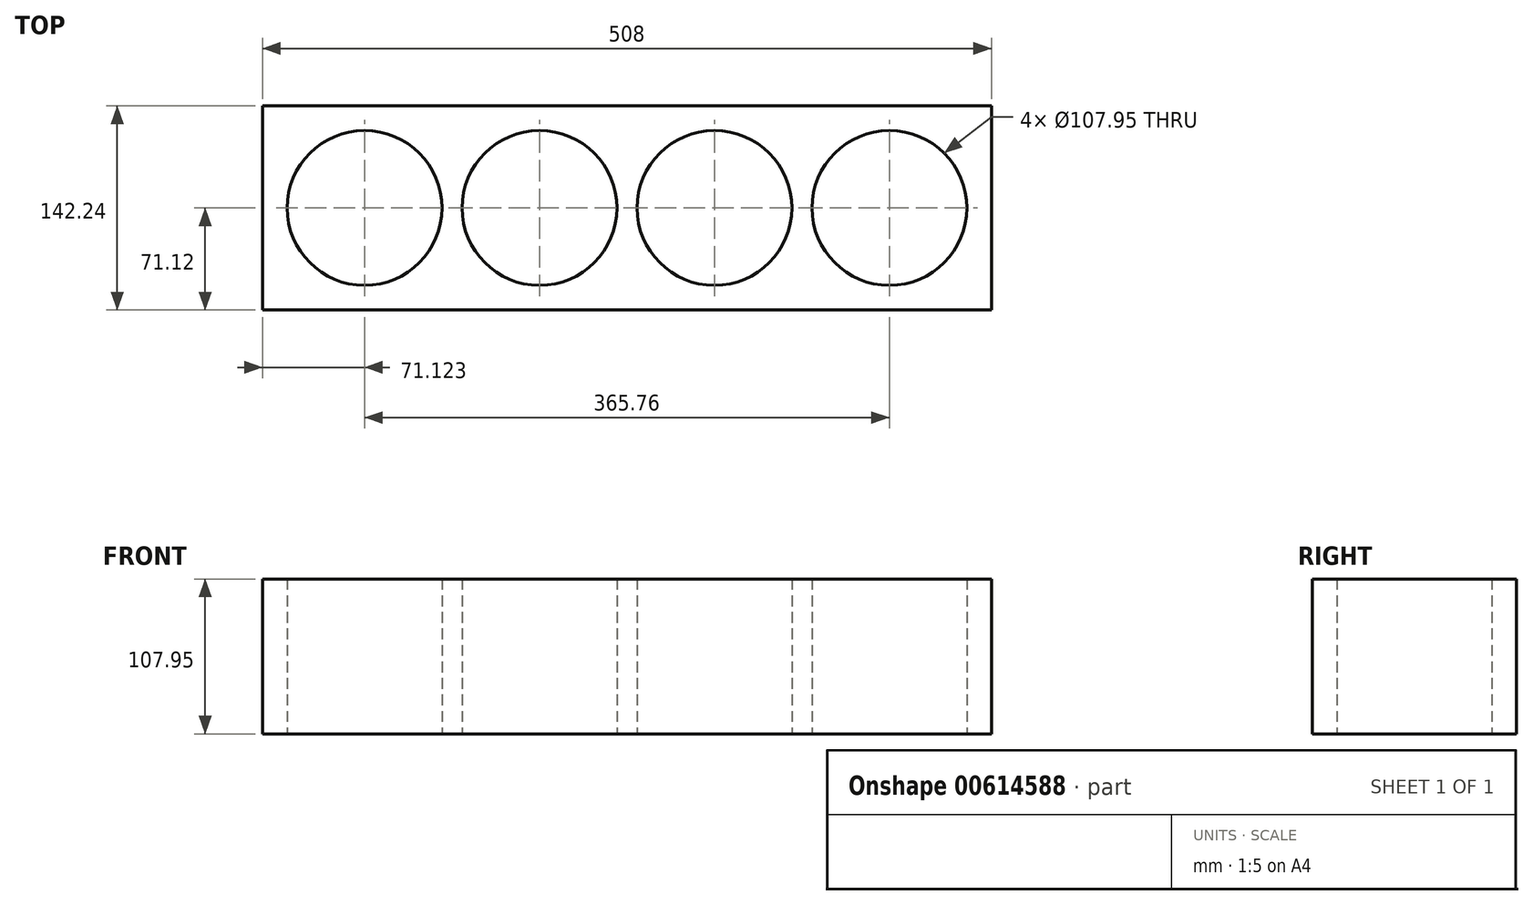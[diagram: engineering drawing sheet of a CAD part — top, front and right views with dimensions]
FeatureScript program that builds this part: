
annotation { "Feature Type Name" : "Feature", "Feature Type Description" : "" }
export const myFeature = defineFeature(function(context is Context, id is Id, definition is map)
    precondition{}
    {
        {
            var Q0;
            Q0=qCreatedBy(makeId("Top.planeOp"),FACE);
            var sketch = newSketch(context, id + "F0", { "sketchPlane" : qUnion([Q0])});
            skCircle(sketch, "E0", {"center": v(-141.8, 0) * mm, "radius": 53.98 * mm});
            skCircle(sketch, "E1.1.0.0", {"center": v(-19.88, 0) * mm, "radius": 53.98 * mm});
            skCircle(sketch, "E1.2.0.0", {"center": v(102.04, 0) * mm, "radius": 53.98 * mm});
            skCircle(sketch, "E1.3.0.0", {"center": v(223.96, 0) * mm, "radius": 53.98 * mm});
            skLineSegment(sketch, "E1.direction1", {"start": v(-141.8, 0) * mm, "end": v(-19.88, 0) * mm, "construction": true});
            skLineSegment(sketch, "E2", {"start": v(-141.8, 0) * mm, "end": v(223.96, 0) * mm, "construction": true});
            skLineSegment(sketch, "E3.bottom", {"start": v(295.08, -71.12) * mm, "end": v(-212.92, -71.12) * mm});
            skLineSegment(sketch, "E3.top", {"start": v(295.08, 71.12) * mm, "end": v(-212.92, 71.12) * mm});
            skLineSegment(sketch, "E3.left", {"start": v(295.08, -71.12) * mm, "end": v(295.08, 71.12) * mm});
            skLineSegment(sketch, "E3.right", {"start": v(-212.92, -71.12) * mm, "end": v(-212.92, 71.12) * mm});
            skPoint(sketch, "E3.middle", {"position": v(41.08, 0) * mm});
            skSolve(sketch);
        }
        {
            var Q0;
            Q0=makeQuery(id+"F0.imprint","IMPRINT",FACE,{"disambiguationData":[TD([[makeQuery(id+"F0.imprint","IMPRINT",EDGE,{"derivedFrom":sQuery(id+"F0.wireOp",EDGE,"E0")}),-1.0]])]});
            extrude(context, id + "F1", {"entities" : qUnion([Q0]), "depth" : 107.95 * mm, "offsetDistance" : 25.4 * mm});
        }
    });
